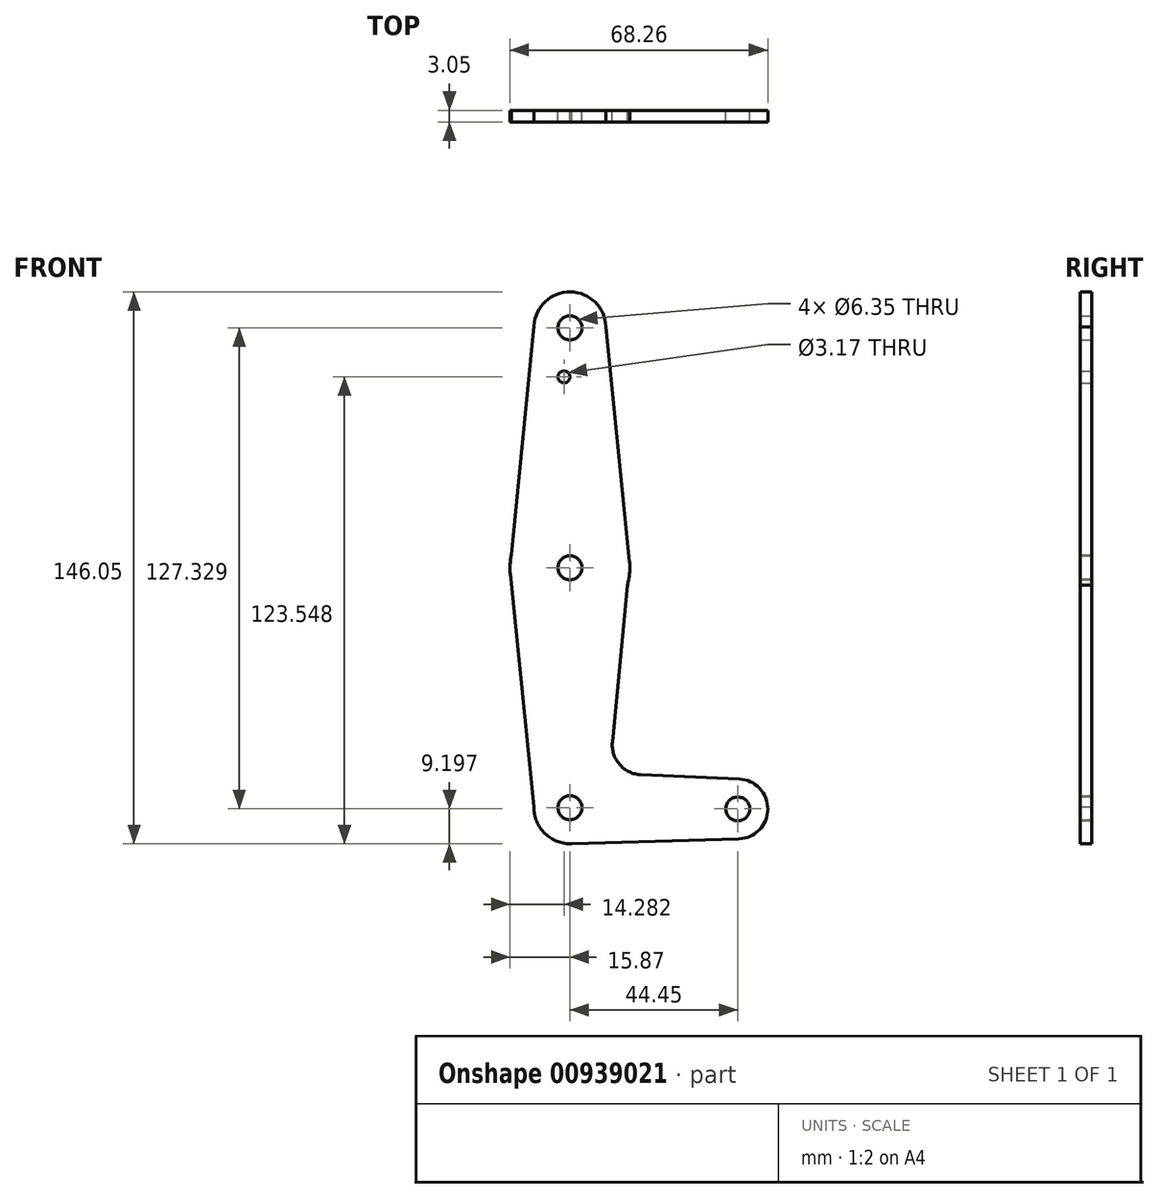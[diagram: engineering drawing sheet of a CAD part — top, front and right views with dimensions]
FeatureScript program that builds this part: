
annotation { "Feature Type Name" : "Feature", "Feature Type Description" : "" }
export const myFeature = defineFeature(function(context is Context, id is Id, definition is map)
    precondition{}
    {
        {
            var Q0;
            Q0=qCreatedBy(makeId("Front.planeOp"),FACE);
            var sketch = newSketch(context, id + "F0", { "sketchPlane" : qUnion([Q0])});
            skCircle(sketch, "E0", {"center": v(0, 99.65) * mm, "radius": 9.53 * mm});
            skCircle(sketch, "E1", {"center": v(0, 36.15) * mm, "radius": 15.88 * mm});
            skCircle(sketch, "E2", {"center": v(0, -27.35) * mm, "radius": 9.53 * mm});
            skCircle(sketch, "E3", {"center": v(44.45, -27.68) * mm, "radius": 7.94 * mm});
            skLineSegment(sketch, "E4", {"start": v(9.52, 99.95) * mm, "end": v(15.8, 37.74) * mm});
            skLineSegment(sketch, "E5", {"start": v(-9.5, 100.18) * mm, "end": v(-15.87, 35.85) * mm});
            skLineSegment(sketch, "E6", {"start": v(15.8, 37.74) * mm, "end": v(11.23, -9.94) * mm});
            skLineSegment(sketch, "E7", {"start": v(-15.87, 35.85) * mm, "end": v(-9.52, -27.1) * mm});
            skLineSegment(sketch, "E8", {"start": v(18.8, -18.64) * mm, "end": v(44.8, -19.75) * mm});
            skLineSegment(sketch, "E9", {"start": v(0, -36.88) * mm, "end": v(44.67, -35.62) * mm});
            skCircle(sketch, "E10", {"center": v(0, 99.65) * mm, "radius": 3.18 * mm});
            skCircle(sketch, "E11", {"center": v(-1.59, 86.67) * mm, "radius": 1.59 * mm});
            skCircle(sketch, "E12", {"center": v(0, 36.15) * mm, "radius": 3.18 * mm});
            skCircle(sketch, "E13", {"center": v(0, -27.35) * mm, "radius": 3.18 * mm});
            skCircle(sketch, "E14", {"center": v(44.45, -27.68) * mm, "radius": 3.18 * mm});
            skPoint(sketch, "E15.newPointB", {"position": v(0, -17.83) * mm});
            skArc(sketch, "E15.filletArc", {"start": v(11.23, -9.94) * mm, "mid": v(13.15, -15.91) * mm, "end": v(18.8, -18.64) * mm});
            skSolve(sketch);
        }
        {
            var Q0;
            Q0 = qSketchRegion(id + "F0", true);
            extrude(context, id + "F1", {"entities" : qUnion([Q0]), "depth" : 3.05 * mm, "offsetDistance" : 25.4 * mm});
        }
    });
